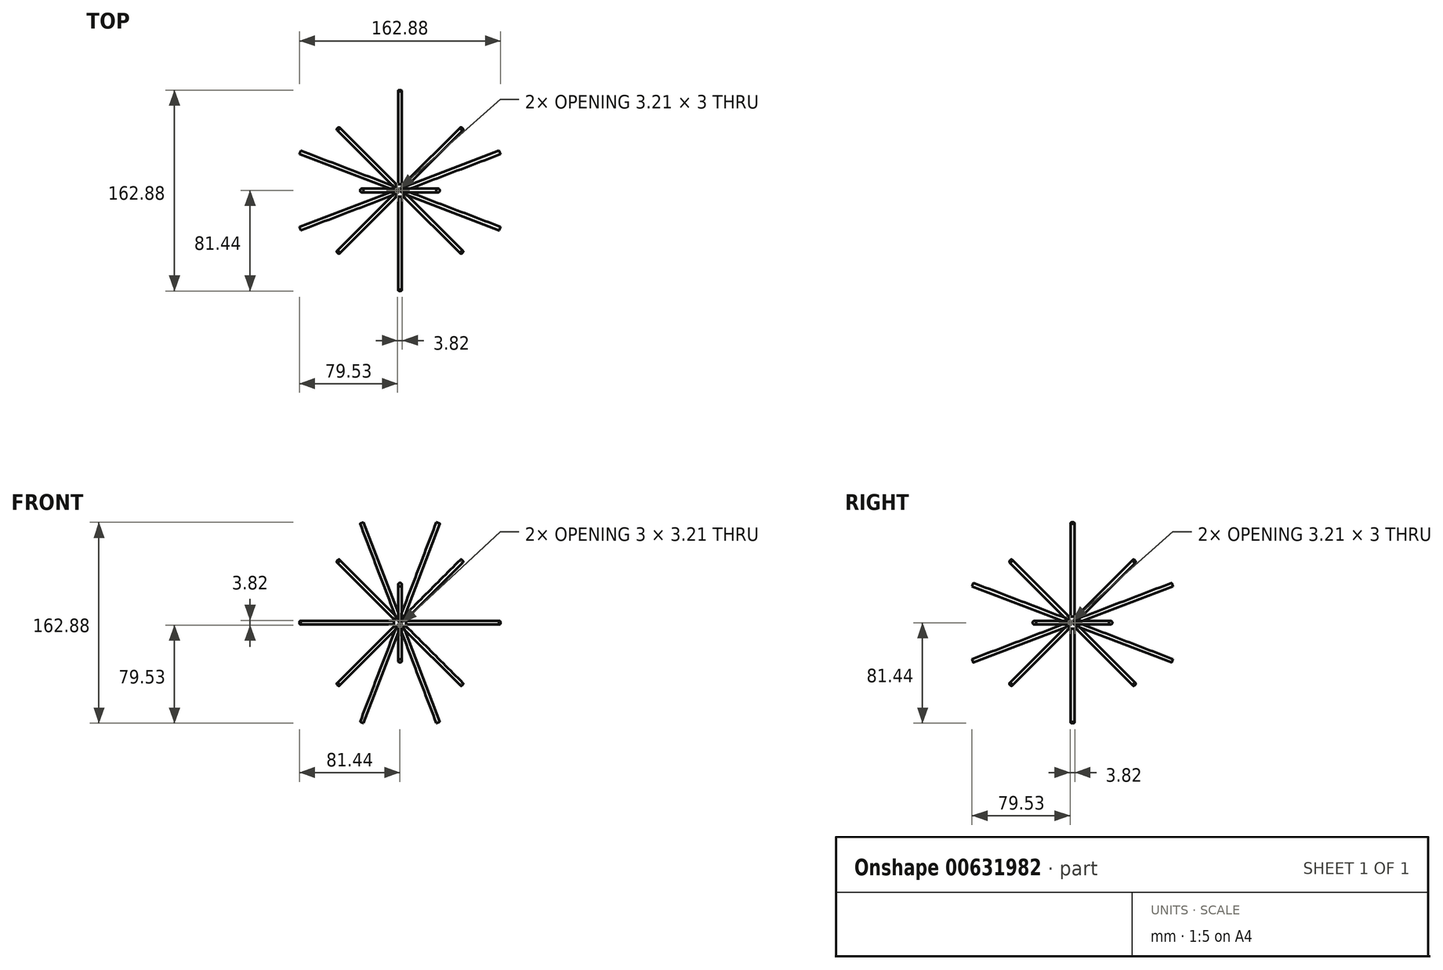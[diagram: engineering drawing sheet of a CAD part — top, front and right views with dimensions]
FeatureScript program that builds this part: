
annotation { "Feature Type Name" : "Feature", "Feature Type Description" : "" }
export const myFeature = defineFeature(function(context is Context, id is Id, definition is map)
    precondition{}
    {
        {
            var Q0;
            Q0=qCreatedBy(makeId("Top.planeOp"),FACE);
            var sketch = newSketch(context, id + "F0", { "sketchPlane" : qUnion([Q0])});
            skLineSegment(sketch, "E0.bottom", {"start": v(5, -5) * mm, "end": v(-5, -5) * mm});
            skLineSegment(sketch, "E0.top", {"start": v(5, 5) * mm, "end": v(-5, 5) * mm});
            skLineSegment(sketch, "E0.left", {"start": v(5, -5) * mm, "end": v(5, 5) * mm});
            skLineSegment(sketch, "E0.right", {"start": v(-5, -5) * mm, "end": v(-5, 5) * mm});
            skPoint(sketch, "E0.middle", {"position": v(0, 0) * mm});
            skLineSegment(sketch, "E1.bottom", {"start": v(80.9, -30.9) * mm, "end": v(-80.9, -30.9) * mm});
            skLineSegment(sketch, "E1.top", {"start": v(80.9, 30.9) * mm, "end": v(-80.9, 30.9) * mm});
            skLineSegment(sketch, "E1.left", {"start": v(80.9, -30.9) * mm, "end": v(80.9, 30.9) * mm});
            skLineSegment(sketch, "E1.right", {"start": v(-80.9, -30.9) * mm, "end": v(-80.9, 30.9) * mm});
            skLineSegment(sketch, "E2", {"start": v(-80.9, 30.9) * mm, "end": v(80.9, -30.9) * mm});
            skLineSegment(sketch, "E3", {"start": v(80.9, 30.9) * mm, "end": v(-80.9, -30.9) * mm});
            skSolve(sketch);
        }
        {
            var Q0;
            Q0=makeQuery(id+"F0.imprint","IMPRINT",FACE,{"disambiguationData":[TD([[makeQuery(id+"F0.imprint","IMPRINT",EDGE,{"derivedFrom":sQuery(id+"F0.wireOp",EDGE,"E0.bottom")}),-1.0]])]});
            var Q1;
            {var subQ0=sQuery(id+"F0.wireOp",EDGE,"E2");var subQ1=sQuery(id+"F0.wireOp",EDGE,"E0.left");var subQ2=makeQuery(id+"F0.imprint","INTERSECT",VERTEX,{"derivedFrom":[subQ1,subQ0]});Q1=makeQuery(id+"F0.imprint","IMPRINT",FACE,{"disambiguationData":[TD([[makeQuery(id+"F0.imprint","IMPRINT",EDGE,{"disambiguationData":[TD([[subQ2,-1.0]])],"derivedFrom":subQ1}),1.0]])]});}
            var Q2;
            {var subQ0=sQuery(id+"F0.wireOp",EDGE,"E3");var subQ1=sQuery(id+"F0.wireOp",EDGE,"E0.right");var subQ2=makeQuery(id+"F0.imprint","INTERSECT",VERTEX,{"derivedFrom":[subQ1,subQ0]});Q2=makeQuery(id+"F0.imprint","IMPRINT",FACE,{"disambiguationData":[TD([[makeQuery(id+"F0.imprint","IMPRINT",EDGE,{"disambiguationData":[TD([[subQ2,-1.0]])],"derivedFrom":subQ1}),-1.0]])]});}
            var Q3;
            {var subQ5=sQuery(id+"F0.wireOp",EDGE,"E0.top");Q3=makeQuery(id+"F0.imprint","IMPRINT",FACE,{"disambiguationData":[TD([[makeQuery(id+"F0.imprint","IMPRINT",EDGE,{"derivedFrom":subQ5}),1.0]])]});}
            extrude(context, id + "F1", {"entities" : qUnion([Q0, Q1, Q2, Q3]), "depth" : 10 * mm, "offsetDistance" : 25 * mm, "symmetric" : true});
        }
        {
            var Q0;
            Q0=makeQuery(id+"F1.opExtrude","CAP_VERTEX",VERTEX,{"disambiguationData":[OSD([sQuery(id+"F0.wireOp",EDGE,"E0.bottom"),sQuery(id+"F0.wireOp",EDGE,"E0.left")])],"isStart":true});
            var Q1;
            Q1=makeQuery(id+"F1.opExtrude","CAP_VERTEX",VERTEX,{"disambiguationData":[OSD([sQuery(id+"F0.wireOp",EDGE,"E0.bottom"),sQuery(id+"F0.wireOp",EDGE,"E0.left")])],"isStart":false});
            var Q2;
            Q2=makeQuery(id+"F1.opExtrude","CAP_VERTEX",VERTEX,{"disambiguationData":[OSD([sQuery(id+"F0.wireOp",EDGE,"E0.top"),sQuery(id+"F0.wireOp",EDGE,"E0.right")])],"isStart":false});
            cPlane(context, id + "F2", {"entities" : qUnion([Q0, Q1, Q2]), "cplaneType" : CPlaneType.THREE_POINT, "offset" : 25 * mm, "width" : 150 * mm, "height" : 150 * mm});
        }
        {
            var Q0;
            Q0=qCreatedBy(id+"F2.planeOp",FACE);
            var sketch = newSketch(context, id + "F3", { "sketchPlane" : qUnion([Q0])});
            skLineSegment(sketch, "E4.bottom", {"start": v(-70.71, -50) * mm, "end": v(70.71, -50) * mm});
            skLineSegment(sketch, "E4.top", {"start": v(-70.71, 50) * mm, "end": v(70.71, 50) * mm});
            skLineSegment(sketch, "E4.left", {"start": v(-70.71, -50) * mm, "end": v(-70.71, 50) * mm});
            skLineSegment(sketch, "E4.right", {"start": v(70.71, -50) * mm, "end": v(70.71, 50) * mm});
            skPoint(sketch, "E4.middle", {"position": v(0, 0) * mm});
            skLineSegment(sketch, "E5", {"start": v(-70.71, 50) * mm, "end": v(70.71, -50) * mm});
            skLineSegment(sketch, "E6", {"start": v(-70.71, -50) * mm, "end": v(70.71, 50) * mm});
            skSolve(sketch);
        }
        {
            var Q0;
            Q0=makeQuery(id+"F1.opExtrude","CAP_VERTEX",VERTEX,{"disambiguationData":[OSD([sQuery(id+"F0.wireOp",EDGE,"E0.bottom"),sQuery(id+"F0.wireOp",EDGE,"E0.right")])],"isStart":true});
            var Q1;
            Q1=makeQuery(id+"F1.opExtrude","CAP_VERTEX",VERTEX,{"disambiguationData":[OSD([sQuery(id+"F0.wireOp",EDGE,"E0.bottom"),sQuery(id+"F0.wireOp",EDGE,"E0.right")])],"isStart":false});
            var Q2;
            Q2=makeQuery(id+"F1.opExtrude","CAP_VERTEX",VERTEX,{"disambiguationData":[OSD([sQuery(id+"F0.wireOp",EDGE,"E0.top"),sQuery(id+"F0.wireOp",EDGE,"E0.left")])],"isStart":false});
            cPlane(context, id + "F4", {"entities" : qUnion([Q0, Q1, Q2]), "cplaneType" : CPlaneType.THREE_POINT, "offset" : 25 * mm, "width" : 150 * mm, "height" : 150 * mm});
        }
        {
            var Q0;
            Q0=qCreatedBy(id+"F4.planeOp",FACE);
            var sketch = newSketch(context, id + "F5", { "sketchPlane" : qUnion([Q0])});
            skLineSegment(sketch, "E7.bottom", {"start": v(70.71, -50) * mm, "end": v(-70.71, -50) * mm});
            skLineSegment(sketch, "E7.top", {"start": v(70.71, 50) * mm, "end": v(-70.71, 50) * mm});
            skLineSegment(sketch, "E7.left", {"start": v(70.71, -50) * mm, "end": v(70.71, 50) * mm});
            skLineSegment(sketch, "E7.right", {"start": v(-70.71, -50) * mm, "end": v(-70.71, 50) * mm});
            skPoint(sketch, "E7.middle", {"position": v(0, 0) * mm});
            skLineSegment(sketch, "E8", {"start": v(70.71, 50) * mm, "end": v(-70.71, -50) * mm});
            skLineSegment(sketch, "E9", {"start": v(70.71, -50) * mm, "end": v(-70.71, 50) * mm});
            skSolve(sketch);
        }
        {
            var Q0;
            Q0=qCreatedBy(makeId("Front.planeOp"),FACE);
            var sketch = newSketch(context, id + "F6", { "sketchPlane" : qUnion([Q0])});
            skLineSegment(sketch, "E10.bottom", {"start": v(30.9, -80.9) * mm, "end": v(-30.9, -80.9) * mm});
            skLineSegment(sketch, "E10.top", {"start": v(30.9, 80.9) * mm, "end": v(-30.9, 80.9) * mm});
            skLineSegment(sketch, "E10.left", {"start": v(30.9, -80.9) * mm, "end": v(30.9, 80.9) * mm});
            skLineSegment(sketch, "E10.right", {"start": v(-30.9, -80.9) * mm, "end": v(-30.9, 80.9) * mm});
            skPoint(sketch, "E10.middle", {"position": v(0, 0) * mm});
            skLineSegment(sketch, "E11", {"start": v(-30.9, 80.9) * mm, "end": v(30.9, -80.9) * mm});
            skLineSegment(sketch, "E12", {"start": v(-30.9, -80.9) * mm, "end": v(30.9, 80.9) * mm});
            skSolve(sketch);
        }
        {
            var Q0;
            Q0=qCreatedBy(makeId("Right.planeOp"),FACE);
            var sketch = newSketch(context, id + "F7", { "sketchPlane" : qUnion([Q0])});
            skLineSegment(sketch, "E13.bottom", {"start": v(80.9, -30.9) * mm, "end": v(-80.9, -30.9) * mm});
            skLineSegment(sketch, "E13.top", {"start": v(80.9, 30.9) * mm, "end": v(-80.9, 30.9) * mm});
            skLineSegment(sketch, "E13.left", {"start": v(80.9, -30.9) * mm, "end": v(80.9, 30.9) * mm});
            skLineSegment(sketch, "E13.right", {"start": v(-80.9, -30.9) * mm, "end": v(-80.9, 30.9) * mm});
            skPoint(sketch, "E13.middle", {"position": v(0, 0) * mm});
            skLineSegment(sketch, "E14", {"start": v(-80.9, -30.9) * mm, "end": v(80.9, 30.9) * mm});
            skLineSegment(sketch, "E15", {"start": v(-80.9, 30.9) * mm, "end": v(80.9, -30.9) * mm});
            skSolve(sketch);
        }
        {
            var Q0;
            Q0=sQuery(id+"F3.wireOp",EDGE,"E5");
            var Q1;
            Q1=sQuery(id+"F3.wireOp",VERTEX,"E5.start");
            cPlane(context, id + "F8", {"entities" : qUnion([Q0, Q1]), "cplaneType" : CPlaneType.LINE_POINT, "offset" : 25 * mm, "width" : 150 * mm, "height" : 150 * mm});
        }
        {
            var Q0;
            Q0=qCreatedBy(id+"F8.planeOp",FACE);
            var sketch = newSketch(context, id + "F9", { "sketchPlane" : qUnion([Q0])});
            skCircle(sketch, "E16", {"center": v(0, 0) * mm, "radius": 1.5 * mm});
            skSolve(sketch);
        }
        {
            var Q0;
            Q0=makeQuery(id+"F9.imprint","IMPRINT",FACE,{"disambiguationData":[TD([[makeQuery(id+"F9.imprint","IMPRINT",EDGE,{"derivedFrom":sQuery(id+"F9.wireOp",EDGE,"E16")}),1.0]])]});
            var Q1;
            Q1=sQuery(id+"F3.wireOp",EDGE,"E5");
            sweep(context, id + "F10", {"operationType" : NewBodyOperationType.ADD, "profiles" : qUnion([Q0]), "path" : qUnion([Q1])});
        }
        {
            var Q0;
            Q0=sQuery(id+"F3.wireOp",EDGE,"E6");
            var Q1;
            Q1=sQuery(id+"F3.wireOp",VERTEX,"E6.start");
            cPlane(context, id + "F11", {"entities" : qUnion([Q0, Q1]), "cplaneType" : CPlaneType.LINE_POINT, "offset" : 25 * mm, "width" : 150 * mm, "height" : 150 * mm});
        }
        {
            var Q0;
            Q0=qCreatedBy(id+"F11.planeOp",FACE);
            var sketch = newSketch(context, id + "F12", { "sketchPlane" : qUnion([Q0])});
            skCircle(sketch, "E17", {"center": v(0, 0) * mm, "radius": 1.5 * mm});
            skSolve(sketch);
        }
        {
            var Q0;
            Q0=makeQuery(id+"F12.imprint","IMPRINT",FACE,{"disambiguationData":[TD([[makeQuery(id+"F12.imprint","IMPRINT",EDGE,{"derivedFrom":sQuery(id+"F12.wireOp",EDGE,"E17")}),1.0]])]});
            var Q1;
            Q1=sQuery(id+"F3.wireOp",EDGE,"E6");
            sweep(context, id + "F13", {"operationType" : NewBodyOperationType.ADD, "profiles" : qUnion([Q0]), "path" : qUnion([Q1])});
        }
        {
            var Q0;
            Q0=sQuery(id+"F5.wireOp",EDGE,"E9");
            var Q1;
            Q1=sQuery(id+"F5.wireOp",VERTEX,"E7.top.end");
            cPlane(context, id + "F14", {"entities" : qUnion([Q0, Q1]), "cplaneType" : CPlaneType.LINE_POINT, "offset" : 25 * mm, "width" : 150 * mm, "height" : 150 * mm});
        }
        {
            var Q0;
            Q0=qCreatedBy(id+"F14.planeOp",FACE);
            var sketch = newSketch(context, id + "F15", { "sketchPlane" : qUnion([Q0])});
            skCircle(sketch, "E18", {"center": v(0, 0) * mm, "radius": 1.5 * mm});
            skSolve(sketch);
        }
        {
            var Q0;
            Q0=makeQuery(id+"F15.imprint","IMPRINT",FACE,{"disambiguationData":[TD([[makeQuery(id+"F15.imprint","IMPRINT",EDGE,{"derivedFrom":sQuery(id+"F15.wireOp",EDGE,"E18")}),1.0]])]});
            var Q1;
            Q1=sQuery(id+"F5.wireOp",EDGE,"E9");
            sweep(context, id + "F16", {"operationType" : NewBodyOperationType.ADD, "profiles" : qUnion([Q0]), "path" : qUnion([Q1])});
        }
        {
            var Q0;
            Q0=sQuery(id+"F5.wireOp",EDGE,"E8");
            var Q1;
            Q1=sQuery(id+"F5.wireOp",VERTEX,"E7.right.start");
            cPlane(context, id + "F17", {"entities" : qUnion([Q0, Q1]), "cplaneType" : CPlaneType.LINE_POINT, "offset" : 25 * mm, "width" : 150 * mm, "height" : 150 * mm});
        }
        {
            var Q0;
            Q0=qCreatedBy(id+"F17.planeOp",FACE);
            var sketch = newSketch(context, id + "F18", { "sketchPlane" : qUnion([Q0])});
            skCircle(sketch, "E19", {"center": v(0, 0) * mm, "radius": 1.5 * mm});
            skSolve(sketch);
        }
        {
            var Q0;
            Q0=makeQuery(id+"F18.imprint","IMPRINT",FACE,{"disambiguationData":[TD([[makeQuery(id+"F18.imprint","IMPRINT",EDGE,{"derivedFrom":sQuery(id+"F18.wireOp",EDGE,"E19")}),1.0]])]});
            var Q1;
            Q1=sQuery(id+"F5.wireOp",EDGE,"E8");
            sweep(context, id + "F19", {"operationType" : NewBodyOperationType.ADD, "profiles" : qUnion([Q0]), "path" : qUnion([Q1])});
        }
        {
            var Q0;
            Q0=sQuery(id+"F7.wireOp",EDGE,"E14");
            var Q1;
            Q1=sQuery(id+"F7.wireOp",VERTEX,"E13.right.start");
            cPlane(context, id + "F20", {"entities" : qUnion([Q0, Q1]), "cplaneType" : CPlaneType.LINE_POINT, "offset" : 25 * mm, "width" : 150 * mm, "height" : 150 * mm});
        }
        {
            var Q0;
            Q0=qCreatedBy(id+"F20.planeOp",FACE);
            var sketch = newSketch(context, id + "F21", { "sketchPlane" : qUnion([Q0])});
            skCircle(sketch, "E20", {"center": v(0, 0) * mm, "radius": 1.5 * mm});
            skSolve(sketch);
        }
        {
            var Q0;
            Q0 = qSketchRegion(id + "F21", true);
            var Q1;
            Q1=sQuery(id+"F7.wireOp",EDGE,"E14");
            sweep(context, id + "F22", {"operationType" : NewBodyOperationType.ADD, "profiles" : qUnion([Q0]), "path" : qUnion([Q1])});
        }
        {
            var Q0;
            Q0=sQuery(id+"F7.wireOp",EDGE,"E15");
            var Q1;
            Q1=sQuery(id+"F7.wireOp",VERTEX,"E13.left.start");
            cPlane(context, id + "F23", {"entities" : qUnion([Q0, Q1]), "cplaneType" : CPlaneType.LINE_POINT, "offset" : 25 * mm, "width" : 150 * mm, "height" : 150 * mm});
        }
        {
            var Q0;
            Q0=qCreatedBy(id+"F23.planeOp",FACE);
            var sketch = newSketch(context, id + "F24", { "sketchPlane" : qUnion([Q0])});
            skCircle(sketch, "E21", {"center": v(0, 0) * mm, "radius": 1.5 * mm});
            skSolve(sketch);
        }
        {
            var Q0;
            Q0=makeQuery(id+"F24.imprint","IMPRINT",FACE,{"disambiguationData":[TD([[makeQuery(id+"F24.imprint","IMPRINT",EDGE,{"derivedFrom":sQuery(id+"F24.wireOp",EDGE,"E21")}),1.0]])]});
            var Q1;
            Q1=sQuery(id+"F7.wireOp",EDGE,"E15");
            sweep(context, id + "F25", {"operationType" : NewBodyOperationType.ADD, "profiles" : qUnion([Q0]), "path" : qUnion([Q1])});
        }
        {
            var Q0;
            Q0=sQuery(id+"F0.wireOp",VERTEX,"E2.end");
            var Q1;
            Q1=sQuery(id+"F0.wireOp",EDGE,"E2");
            cPlane(context, id + "F26", {"entities" : qUnion([Q0, Q1]), "cplaneType" : CPlaneType.LINE_POINT, "offset" : 25 * mm, "width" : 150 * mm, "height" : 150 * mm});
        }
        {
            var Q0;
            Q0=sQuery(id+"F0.wireOp",EDGE,"E3");
            var Q1;
            Q1=sQuery(id+"F0.wireOp",VERTEX,"E3.start");
            cPlane(context, id + "F27", {"entities" : qUnion([Q0, Q1]), "cplaneType" : CPlaneType.LINE_POINT, "offset" : 25 * mm, "width" : 150 * mm, "height" : 150 * mm});
        }
        {
            var Q0;
            Q0=qCreatedBy(id+"F27.planeOp",FACE);
            var sketch = newSketch(context, id + "F28", { "sketchPlane" : qUnion([Q0])});
            skCircle(sketch, "E22", {"center": v(0, 0) * mm, "radius": 1.5 * mm});
            skSolve(sketch);
        }
        {
            var Q0;
            Q0=makeQuery(id+"F28.imprint","IMPRINT",FACE,{"disambiguationData":[TD([[makeQuery(id+"F28.imprint","IMPRINT",EDGE,{"derivedFrom":sQuery(id+"F28.wireOp",EDGE,"E22")}),1.0]])]});
            var Q1;
            Q1=sQuery(id+"F0.wireOp",EDGE,"E3");
            sweep(context, id + "F29", {"operationType" : NewBodyOperationType.ADD, "profiles" : qUnion([Q0]), "path" : qUnion([Q1])});
        }
        {
            var Q0;
            Q0=sQuery(id+"F6.wireOp",EDGE,"E12");
            var Q1;
            Q1=sQuery(id+"F6.wireOp",VERTEX,"E12.end");
            cPlane(context, id + "F30", {"entities" : qUnion([Q0, Q1]), "cplaneType" : CPlaneType.LINE_POINT, "offset" : 25 * mm, "width" : 150 * mm, "height" : 150 * mm});
        }
        {
            var Q0;
            Q0=qCreatedBy(id+"F30.planeOp",FACE);
            var sketch = newSketch(context, id + "F31", { "sketchPlane" : qUnion([Q0])});
            skCircle(sketch, "E23", {"center": v(0, 0) * mm, "radius": 1.5 * mm});
            skSolve(sketch);
        }
        {
            var Q0;
            Q0=qCreatedBy(id+"F26.planeOp",FACE);
            var sketch = newSketch(context, id + "F32", { "sketchPlane" : qUnion([Q0])});
            skCircle(sketch, "E24", {"center": v(0, 0) * mm, "radius": 1.5 * mm});
            skSolve(sketch);
        }
        {
            var Q0;
            Q0=makeQuery(id+"F32.imprint","IMPRINT",FACE,{"disambiguationData":[TD([[makeQuery(id+"F32.imprint","IMPRINT",EDGE,{"derivedFrom":sQuery(id+"F32.wireOp",EDGE,"E24")}),1.0]])]});
            var Q1;
            Q1=sQuery(id+"F0.wireOp",EDGE,"E2");
            sweep(context, id + "F33", {"operationType" : NewBodyOperationType.ADD, "profiles" : qUnion([Q0]), "path" : qUnion([Q1])});
        }
        {
            var Q0;
            Q0=makeQuery(id+"F31.imprint","IMPRINT",FACE,{"disambiguationData":[TD([[makeQuery(id+"F31.imprint","IMPRINT",EDGE,{"derivedFrom":sQuery(id+"F31.wireOp",EDGE,"E23")}),1.0]])]});
            var Q1;
            Q1=sQuery(id+"F6.wireOp",EDGE,"E12");
            sweep(context, id + "F34", {"operationType" : NewBodyOperationType.ADD, "profiles" : qUnion([Q0]), "path" : qUnion([Q1])});
        }
        {
            var Q0;
            Q0=sQuery(id+"F6.wireOp",VERTEX,"E11.start");
            var Q1;
            Q1=sQuery(id+"F6.wireOp",EDGE,"E11");
            cPlane(context, id + "F35", {"entities" : qUnion([Q0, Q1]), "cplaneType" : CPlaneType.LINE_POINT, "offset" : 25 * mm, "width" : 150 * mm, "height" : 150 * mm});
        }
        {
            var Q0;
            Q0=qCreatedBy(id+"F35.planeOp",FACE);
            var sketch = newSketch(context, id + "F36", { "sketchPlane" : qUnion([Q0])});
            skCircle(sketch, "E25", {"center": v(0, 0) * mm, "radius": 1.5 * mm});
            skSolve(sketch);
        }
        {
            var Q0;
            Q0=makeQuery(id+"F36.imprint","IMPRINT",FACE,{"disambiguationData":[TD([[makeQuery(id+"F36.imprint","IMPRINT",EDGE,{"derivedFrom":sQuery(id+"F36.wireOp",EDGE,"E25")}),1.0]])]});
            var Q1;
            Q1=sQuery(id+"F6.wireOp",EDGE,"E11");
            sweep(context, id + "F37", {"operationType" : NewBodyOperationType.ADD, "profiles" : qUnion([Q0]), "path" : qUnion([Q1])});
        }
    });
